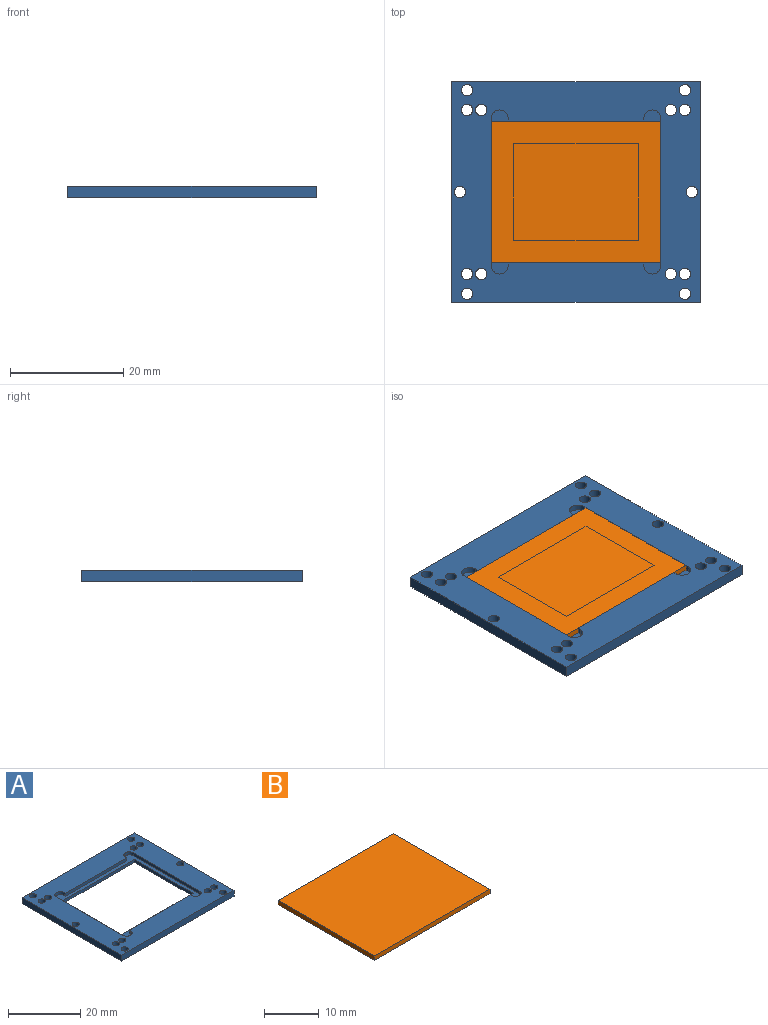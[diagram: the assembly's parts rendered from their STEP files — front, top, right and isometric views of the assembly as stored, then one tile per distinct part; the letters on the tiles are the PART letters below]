
ASSEMBLY  parts=2 mates=1
PART A: 37 faces, bbox 44x39x2 mm
  f0: plane 44x39mm, normal (0,0,1), area 901.9mm2, adj f2,f3,f4,f5,f10,f11,f12,f13
  f1: plane 44x39mm, normal (0,0,-1), area 1028mm2, adj f2,f3,f4,f5,f6,f7,f8,f9
  f2: plane 39x2mm, normal (-1,0,0), area 78mm2, adj f0,f1,f3,f5
  f3: plane 44x2mm, normal (0,-1,0), area 88mm2, adj f0,f1,f2,f4
  f4: plane 39x2mm, normal (1,0,0), area 78mm2, adj f0,f1,f3,f5
  f5: plane 44x2mm, normal (0,1,0), area 88mm2, adj f0,f1,f2,f4
  f6: plane 23x1mm, normal (-1,0,0), area 23mm2, adj f1,f7,f9,f22
  f7: plane 28x1mm, normal (0,-1,0), area 28mm2, adj f1,f6,f8,f22
  f8: plane 23x1mm, normal (1,0,0), area 23mm2, adj f1,f7,f9,f22
  f9: plane 28x1mm, normal (0,1,0), area 28mm2, adj f1,f6,f8,f22
  f10: cylinder r=1.5mm len=3mm, axis (0,0,1), area 4.7mm2, adj f0,f11,f21,f22
  f11: plane 1x0.5mm, normal (-1,0,0), area 0.5mm2, adj f0,f10,f12,f22
  f12: plane 24x1mm, normal (0,-1,0), area 24mm2, adj f0,f11,f13,f22
  f13: plane 1x0.5mm, normal (1,0,0), area 0.5mm2, adj f0,f12,f14,f22
  f14: cylinder r=1.5mm len=3mm, axis (0,0,1), area 4.7mm2, adj f0,f13,f15,f22
  f15: plane 26x1mm, normal (-1,0,0), area 26mm2, adj f0,f14,f16,f22
  f16: cylinder r=1.5mm len=3mm, axis (0,0,1), area 4.7mm2, adj f0,f15,f17,f22
  f17: plane 1x0.5mm, normal (1,0,0), area 0.5mm2, adj f0,f16,f18,f22
  f18: plane 24x1mm, normal (0,1,0), area 24mm2, adj f0,f17,f19,f22
  f19: plane 1x0.5mm, normal (-1,0,0), area 0.5mm2, adj f0,f18,f20,f22
  f20: cylinder r=1.5mm len=3mm, axis (0,0,1), area 4.7mm2, adj f0,f19,f21,f22
  f21: plane 26x1mm, normal (1,0,0), area 26mm2, adj f0,f10,f20,f22
  f22: plane 30x29mm, normal (0,0,1), area 126.1mm2, adj f6,f7,f8,f9,f10,f11,f12,f13
  f23: cylinder r=1mm len=2mm, axis (0,0,-1), area 12.6mm2, adj f0,f1
  f24: cylinder r=1mm len=2mm, axis (0,0,-1), area 12.6mm2, adj f0,f1
  f25: cylinder r=1mm len=2mm, axis (0,0,-1), area 12.6mm2, adj f0,f1
  f26: cylinder r=1mm len=2mm, axis (0,0,-1), area 12.6mm2, adj f0,f1
  f27: cylinder r=1mm len=2mm, axis (0,0,-1), area 12.6mm2, adj f0,f1
  f28: cylinder r=1mm len=2mm, axis (0,0,-1), area 12.6mm2, adj f0,f1
  f29: cylinder r=1mm len=2mm, axis (0,0,-1), area 12.6mm2, adj f0,f1
  f30: cylinder r=1mm len=2mm, axis (0,0,-1), area 12.6mm2, adj f0,f1
  f31: cylinder r=1mm len=2mm, axis (0,0,-1), area 12.6mm2, adj f0,f1
  f32: cylinder r=1mm len=2mm, axis (0,0,-1), area 12.6mm2, adj f0,f1
  f33: cylinder r=1mm len=2mm, axis (0,0,-1), area 12.6mm2, adj f0,f1
  f34: cylinder r=1mm len=2mm, axis (0,0,-1), area 12.6mm2, adj f0,f1
  f35: cylinder r=1mm len=2mm, axis (0,0,-1), area 12.6mm2, adj f0,f1
  f36: cylinder r=1mm len=2mm, axis (0,0,-1), area 12.6mm2, adj f0,f1
PART B: 11 faces, bbox 30x25x1 mm
  f0: plane 30x25mm, normal (0,0,-1), area 376mm2, adj f2,f3,f4,f5,f6,f7,f8,f9
  f1: plane 30x25mm, normal (0,0,1), area 750mm2, adj f2,f3,f4,f5
  f2: plane 30x1mm, normal (0,-1,0), area 30mm2, adj f0,f1,f3,f4
  f3: plane 25x1mm, normal (1,0,0), area 25mm2, adj f0,f1,f2,f5
  f4: plane 25x1mm, normal (-1,0,0), area 25mm2, adj f0,f1,f2,f5
  f5: plane 30x1mm, normal (0,1,0), area 30mm2, adj f0,f1,f3,f4
  f6: plane 22x0mm, normal (0,1,0), area 0mm2, adj f0,f7,f8,f10
  f7: plane 17x0mm, normal (-1,0,0), area 0mm2, adj f0,f6,f9,f10
  f8: plane 17x0mm, normal (1,0,0), area 0mm2, adj f0,f6,f9,f10
  f9: plane 22x0mm, normal (0,-1,0), area 0mm2, adj f0,f7,f8,f10
  f10: plane 22x17mm, normal (0,0,-1), area 374mm2, adj f6,f7,f8,f9
PLACE A rot(axis=(0,1,0),0deg) t=(0,0,0)mm
PLACE B rot(axis=(0,-1,0),180deg) t=(37,7,1)mm
MATE fastened B.f1 <-> A.f22  axis (0,0,-1) through (22,19.5,1)mm
